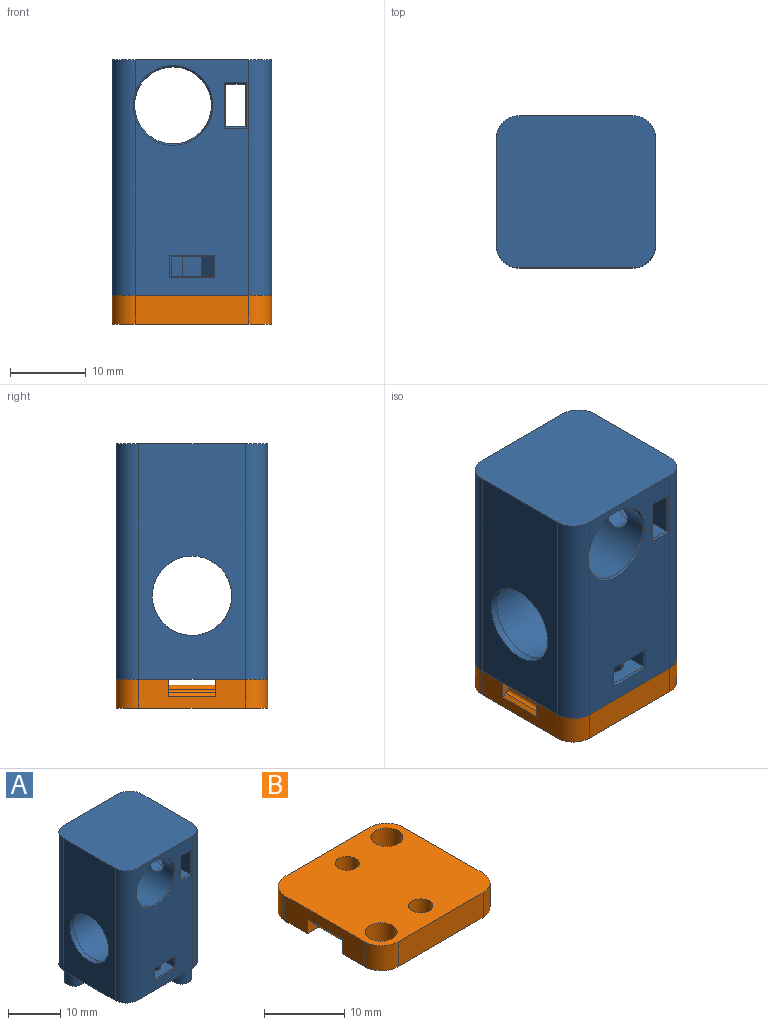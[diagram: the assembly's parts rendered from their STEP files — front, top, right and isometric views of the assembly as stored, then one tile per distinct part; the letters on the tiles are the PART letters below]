
ASSEMBLY  parts=2 mates=1
PART A: 71 faces, bbox 21x20x34.8 mm
  f0: plane 31x15mm, normal (0,1,0), area 343.5mm2, adj f4,f5,f41,f42,f43,f44,f58,f59
  f1: plane 31x15mm, normal (0,-1,0), area 343.5mm2, adj f4,f5,f38,f39,f49,f50,f51,f52
  f2: plane 31x14mm, normal (-1,0,0), area 348.1mm2, adj f4,f5,f7,f63,f64
  f3: plane 31x14mm, normal (1,0,0), area 286.1mm2, adj f4,f5,f54,f65,f66,f69,f70
  f4: plane 21x20mm, normal (0,0,1), area 412.3mm2, adj f0,f1,f2,f3,f63,f64,f65,f66
  f5: plane 21x20mm, normal (0,0,-1), area 370.2mm2, adj f0,f1,f2,f3,f12,f14,f46,f47
  f6: cylinder r=5.06mm len=19.6mm, axis (0,-1,0), area 597.4mm2, adj f57,f58,f67,f68
  f7: cylinder r=5.23mm len=10.46mm, axis (-1,0,0), area 32.9mm2, adj f2,f9
  f8: cylinder r=6.05mm len=19.8mm, axis (-1,0,0), area 752.7mm2, adj f9,f54
  f9: plane 12.1x12.1mm, normal (1,0,0), area 29.1mm2, adj f7,f8
  f10: cylinder r=1.5mm len=3mm, axis (0,0,-1), area 19.8mm2, adj f40,f46
  f11: cylinder r=1.5mm len=3mm, axis (0,0,-1), area 19.8mm2, adj f47,f48
  f12: cylinder r=1.95mm len=3.9mm, axis (0,0,1), area 46.6mm2, adj f5,f13
  f13: plane 3.9x3.9mm, normal (0,0,-1), area 11.9mm2, adj f12
  f14: cylinder r=1.95mm len=3.9mm, axis (0,0,1), area 46.6mm2, adj f5,f15
  f15: plane 3.9x3.9mm, normal (0,0,-1), area 11.9mm2, adj f14
  f16: plane 7.7x5.55mm, normal (0,0,1), area 31.4mm2, adj f18,f19,f20,f30,f31,f48,f50
  f17: plane 7.7x5.55mm, normal (0,0,-1), area 31.4mm2, adj f18,f19,f20,f30,f31,f51,f53
  f18: plane 6.2x2.55mm, normal (1,0,0), area 15.8mm2, adj f16,f17,f31,f52
  f19: plane 6.2x2.55mm, normal (-1,0,0), area 15.8mm2, adj f16,f17,f30,f49
  f20: plane 2.55x2.55mm, normal (0,-1,0), area 6.5mm2, adj f16,f17,f30,f31
  f21: plane 3x3mm, normal (0,0,-1), area 7.1mm2, adj f22
  f22: cylinder r=1.5mm len=3mm, axis (0,0,-1), area 21.2mm2, adj f21,f53
  f23: plane 7.7x5.55mm, normal (0,0,1), area 31.4mm2, adj f25,f26,f27,f32,f33,f40,f42
  f24: plane 7.7x5.55mm, normal (0,0,-1), area 31.4mm2, adj f25,f26,f27,f32,f33,f43,f45
  f25: plane 6.2x2.55mm, normal (-1,0,0), area 15.8mm2, adj f23,f24,f33,f44
  f26: plane 6.2x2.55mm, normal (1,0,0), area 15.8mm2, adj f23,f24,f32,f41
  f27: plane 2.55x2.55mm, normal (0,1,0), area 6.5mm2, adj f23,f24,f32,f33
  f28: plane 3x3mm, normal (0,0,-1), area 7.1mm2, adj f29
  f29: cylinder r=1.5mm len=3mm, axis (0,0,-1), area 21.2mm2, adj f28,f45
  f30: plane 2.55x1.5mm, normal (-0.71,-0.71,0), area 5.4mm2, adj f16,f17,f19,f20
  f31: plane 2.55x1.5mm, normal (0.71,-0.71,0), area 5.4mm2, adj f16,f17,f18,f20
  f32: plane 2.55x1.5mm, normal (0.71,0.71,0), area 5.4mm2, adj f23,f24,f26,f27
  f33: plane 2.55x1.5mm, normal (-0.71,0.71,0), area 5.4mm2, adj f23,f24,f25,f27
  f34: plane 19.6x2.55mm, normal (0,0,-1), area 50mm2, adj f35,f37,f39,f60
  f35: plane 19.6x5.55mm, normal (-1,0,0), area 83.6mm2, adj f34,f36,f56,f62,f69,f70
  f36: plane 19.6x2.55mm, normal (0,0,1), area 50mm2, adj f35,f37,f38,f61
  f37: plane 19.6x5.55mm, normal (1,0,0), area 83.6mm2, adj f34,f36,f55,f59,f67,f68
  f38: plane 2.95x0.2mm, normal (0,-0.71,0.71), area 0.8mm2, adj f1,f36,f55,f56
  f39: plane 2.95x0.2mm, normal (0,-0.71,-0.71), area 0.8mm2, adj f1,f34,f55,f56
  f40: cone r=1.5mm half-angle=45deg, axis (0,0,1), area 2.8mm2, adj f10,f23
  f41: plane 2.95x0.2mm, normal (0.71,0.71,0), area 0.8mm2, adj f0,f26,f42,f43
  f42: plane 5.95x0.2mm, normal (0,0.71,0.71), area 1.6mm2, adj f0,f23,f41,f44
  f43: plane 5.95x0.2mm, normal (0,0.71,-0.71), area 1.6mm2, adj f0,f24,f41,f44
  f44: plane 2.95x0.2mm, normal (-0.71,0.71,0), area 0.8mm2, adj f0,f25,f42,f43
  f45: cone r=1.7mm half-angle=45deg, axis (0,0,-1), area 2.8mm2, adj f24,f29
  f46: cone r=1.5mm half-angle=45deg, axis (0,0,-1), area 2.8mm2, adj f5,f10
  f47: cone r=1.5mm half-angle=45deg, axis (0,0,-1), area 2.8mm2, adj f5,f11
  f48: cone r=1.5mm half-angle=45deg, axis (0,0,1), area 2.8mm2, adj f11,f16
  f49: plane 2.95x0.2mm, normal (-0.71,-0.71,0), area 0.8mm2, adj f1,f19,f50,f51
  f50: plane 5.95x0.2mm, normal (0,-0.71,0.71), area 1.6mm2, adj f1,f16,f49,f52
  f51: plane 5.95x0.2mm, normal (0,-0.71,-0.71), area 1.6mm2, adj f1,f17,f49,f52
  f52: plane 2.95x0.2mm, normal (0.71,-0.71,0), area 0.8mm2, adj f1,f18,f50,f51
  f53: cone r=1.7mm half-angle=45deg, axis (0,0,-1), area 2.8mm2, adj f17,f22
  f54: cone r=6.25mm half-angle=45deg, axis (1,0,0), area 10.9mm2, adj f3,f8
  f55: plane 5.95x0.2mm, normal (0.71,-0.71,0), area 1.6mm2, adj f1,f37,f38,f39
  f56: plane 5.95x0.2mm, normal (-0.71,-0.71,0), area 1.6mm2, adj f1,f35,f38,f39
  f57: cone r=5.06mm half-angle=45deg, axis (0,-1,0), area 9.2mm2, adj f1,f6,f64
  f58: cone r=5.06mm half-angle=45deg, axis (0,1,0), area 9.2mm2, adj f0,f6,f63
  f59: plane 5.95x0.2mm, normal (0.71,0.71,0), area 1.6mm2, adj f0,f37,f60,f61
  f60: plane 2.95x0.2mm, normal (0,0.71,-0.71), area 0.8mm2, adj f0,f34,f59,f62
  f61: plane 2.95x0.2mm, normal (0,0.71,0.71), area 0.8mm2, adj f0,f36,f59,f62
  f62: plane 5.95x0.2mm, normal (-0.71,0.71,0), area 1.6mm2, adj f0,f35,f60,f61
  f63: cylinder r=3mm len=31mm, axis (0,0,1), area 145.5mm2, adj f0,f2,f4,f5,f58
  f64: cylinder r=3mm len=31mm, axis (0,0,-1), area 145.5mm2, adj f1,f2,f4,f5,f57
  f65: cylinder r=3mm len=31mm, axis (0,0,1), area 146.1mm2, adj f1,f3,f4,f5
  f66: cylinder r=3mm len=31mm, axis (0,0,-1), area 146.1mm2, adj f0,f3,f4,f5
  f67: cylinder r=2mm len=4mm, axis (1,0,0), area 26.3mm2, adj f6,f37
  f68: cylinder r=2mm len=4mm, axis (1,0,0), area 26.3mm2, adj f6,f37
  f69: cylinder r=2mm len=4mm, axis (1,0,0), area 44mm2, adj f3,f35
  f70: cylinder r=2mm len=4mm, axis (1,0,0), area 44mm2, adj f3,f35
PART B: 44 faces, bbox 21x20x3.8 mm
  f0: plane 14x3.8mm, normal (1,0,0), area 38.9mm2, adj f4,f5,f6,f26,f33,f34,f37,f38
  f1: plane 15x3.8mm, normal (0,1,0), area 57mm2, adj f4,f33,f35,f38
  f2: plane 14x3.8mm, normal (-1,0,0), area 38.9mm2, adj f4,f5,f6,f33,f34,f35,f36,f39
  f3: plane 15x3.8mm, normal (0,-1,0), area 57mm2, adj f4,f34,f36,f37
  f4: plane 21x20mm, normal (0,0,1), area 373mm2, adj f0,f1,f2,f3,f29,f30,f31,f32
  f5: plane 21x2.3mm, normal (0,1,0), area 28mm2, adj f0,f2,f7,f8,f9,f10,f11,f12
  f6: plane 21x2.3mm, normal (0,-1,0), area 28mm2, adj f0,f2,f7,f8,f9,f10,f11,f12
  f7: cylinder r=0.5mm len=6.2mm, axis (0,-1,0), area 4.9mm2, adj f5,f6,f8,f39
  f8: cylinder r=0.5mm len=6.2mm, axis (0,-1,0), area 9.7mm2, adj f5,f6,f7,f9
  f9: cylinder r=0.5mm len=6.2mm, axis (0,1,0), area 9.7mm2, adj f5,f6,f8,f10
  f10: cylinder r=0.5mm len=6.2mm, axis (0,-1,0), area 9.7mm2, adj f5,f6,f9,f11
  f11: cylinder r=0.5mm len=6.2mm, axis (0,1,0), area 9.7mm2, adj f5,f6,f10,f12
  f12: cylinder r=0.5mm len=6.2mm, axis (0,-1,0), area 9.7mm2, adj f5,f6,f11,f13
  f13: cylinder r=0.5mm len=6.2mm, axis (0,1,0), area 9.7mm2, adj f5,f6,f12,f14
  f14: cylinder r=0.5mm len=6.2mm, axis (0,-1,0), area 9.7mm2, adj f5,f6,f13,f15
  f15: cylinder r=0.5mm len=6.2mm, axis (0,1,0), area 9.7mm2, adj f5,f6,f14,f16
  f16: cylinder r=0.5mm len=6.2mm, axis (0,-1,0), area 9.7mm2, adj f5,f6,f15,f17
  f17: cylinder r=0.5mm len=6.2mm, axis (0,1,0), area 9.7mm2, adj f5,f6,f16,f18
  f18: cylinder r=0.5mm len=6.2mm, axis (0,-1,0), area 9.7mm2, adj f5,f6,f17,f19
  f19: cylinder r=0.5mm len=6.2mm, axis (0,1,0), area 9.7mm2, adj f5,f6,f18,f20
  f20: cylinder r=0.5mm len=6.2mm, axis (0,-1,0), area 9.7mm2, adj f5,f6,f19,f21
  f21: cylinder r=0.5mm len=6.2mm, axis (0,1,0), area 9.7mm2, adj f5,f6,f20,f22
  f22: cylinder r=0.5mm len=6.2mm, axis (0,-1,0), area 9.7mm2, adj f5,f6,f21,f23
  f23: cylinder r=0.5mm len=6.2mm, axis (0,1,0), area 9.7mm2, adj f5,f6,f22,f24
  f24: cylinder r=0.5mm len=6.2mm, axis (0,-1,0), area 9.7mm2, adj f5,f6,f23,f25
  f25: cylinder r=0.5mm len=6.2mm, axis (0,1,0), area 9.7mm2, adj f5,f6,f24,f27
  f26: cylinder r=0.5mm len=6.2mm, axis (0,-1,0), area 4.9mm2, adj f0,f5,f6,f28
  f27: cylinder r=0.5mm len=6.2mm, axis (0,-1,0), area 9.7mm2, adj f5,f6,f25,f28
  f28: cylinder r=0.5mm len=6.2mm, axis (0,1,0), area 4.9mm2, adj f5,f6,f26,f27
  f29: cylinder r=2mm len=4mm, axis (0,0,-1), area 45.2mm2, adj f4,f42
  f30: cylinder r=1.5mm len=3.6mm, axis (0,0,-1), area 33.9mm2, adj f4,f43
  f31: cylinder r=1.5mm len=3.6mm, axis (0,0,-1), area 33.9mm2, adj f4,f41
  f32: cylinder r=2mm len=4mm, axis (0,0,-1), area 45.2mm2, adj f4,f40
  f33: plane 21x6.9mm, normal (0,0,-1), area 116.8mm2, adj f0,f1,f2,f6,f35,f38,f42,f43
  f34: plane 21x6.9mm, normal (0,0,-1), area 116.8mm2, adj f0,f2,f3,f5,f36,f37,f40,f41
  f35: cylinder r=3mm len=3.8mm, axis (0,0,1), area 17.9mm2, adj f1,f2,f4,f33
  f36: cylinder r=3mm len=3.8mm, axis (0,0,-1), area 17.9mm2, adj f2,f3,f4,f34
  f37: cylinder r=3mm len=3.8mm, axis (0,0,1), area 17.9mm2, adj f0,f3,f4,f34
  f38: cylinder r=3mm len=3.8mm, axis (0,0,-1), area 17.9mm2, adj f0,f1,f4,f33
  f39: plane 6.2x0.5mm, normal (-0.71,0,-0.71), area 4.4mm2, adj f2,f5,f6,f7
  f40: cone r=2mm half-angle=45deg, axis (0,0,-1), area 3.7mm2, adj f32,f34
  f41: cone r=1.5mm half-angle=45deg, axis (0,0,-1), area 2.8mm2, adj f31,f34
  f42: cone r=2mm half-angle=45deg, axis (0,0,-1), area 3.7mm2, adj f29,f33
  f43: cone r=1.5mm half-angle=45deg, axis (0,0,-1), area 2.8mm2, adj f30,f33
PLACE A t=(45.98,12.12,-2.42)mm
PLACE B rot(axis=(1,0,0),180deg) t=(106.13,-23.88,-3.22)mm
MATE fastened B.f32 <-> A.f12  axis (0,0,-1) through (38.48,19.12,-6.22)mm
